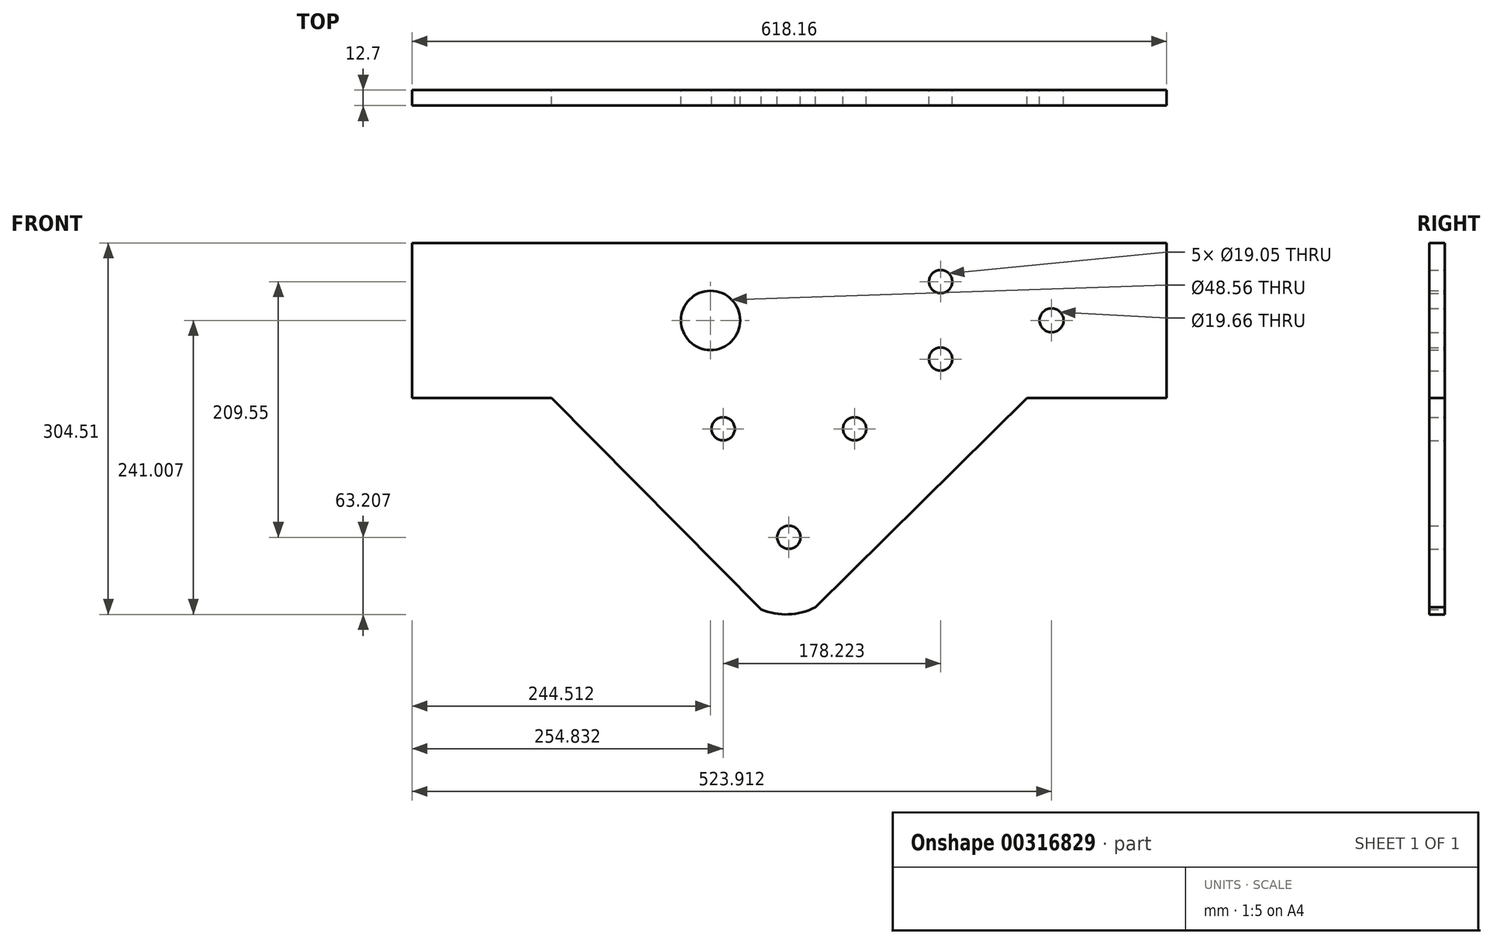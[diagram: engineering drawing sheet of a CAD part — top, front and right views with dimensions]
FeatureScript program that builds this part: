
annotation { "Feature Type Name" : "Feature", "Feature Type Description" : "" }
export const myFeature = defineFeature(function(context is Context, id is Id, definition is map)
    precondition{}
    {
        {
            var Q0;
            Q0=qCreatedBy(makeId("Front.planeOp"),FACE);
            var sketch = newSketch(context, id + "F0", { "sketchPlane" : qUnion([Q0])});
            skLineSegment(sketch, "E0.bottom", {"start": v(-308.68, 55.52) * mm, "end": v(-194.38, 55.52) * mm});
            skLineSegment(sketch, "E0.top", {"start": v(-308.68, 182.52) * mm, "end": v(309.48, 182.52) * mm});
            skLineSegment(sketch, "E0.left", {"start": v(-308.68, 55.52) * mm, "end": v(-308.68, 182.52) * mm});
            skLineSegment(sketch, "E0.right", {"start": v(309.48, 55.52) * mm, "end": v(309.48, 182.52) * mm});
            skLineSegment(sketch, "E1", {"start": v(-158.49, 19.24) * mm, "end": v(-22.68, -118.05) * mm});
            skArc(sketch, "E2", {"start": v(-22.68, -118.05) * mm, "mid": v(-0.3, -121.94) * mm, "end": v(21.65, -116.14) * mm});
            skLineSegment(sketch, "E3.trimOffspring", {"start": v(195.18, 55.52) * mm, "end": v(309.48, 55.52) * mm});
            skCircle(sketch, "E4", {"center": v(-64.17, 119.02) * mm, "radius": 24.28 * mm});
            skCircle(sketch, "E5.MirrorC", {"center": v(215.23, 119.02) * mm, "radius": 9.83 * mm});
            skLineSegment(sketch, "E6.MirrorCS", {"start": v(195.18, 55.52) * mm, "end": v(21.65, -116.14) * mm});
            skLineSegment(sketch, "E7", {"start": v(-308.68, 87.27) * mm, "end": v(309.48, 87.27) * mm, "construction": true});
            skLineSegment(sketch, "E8", {"start": v(-308.68, 150.77) * mm, "end": v(309.48, 150.77) * mm, "construction": true});
            skLineSegment(sketch, "E9", {"start": v(0, 0) * mm, "end": v(0, 29.21) * mm});
            skLineSegment(sketch, "E10.0", {"start": v(53.85, 0) * mm, "end": v(53.85, 30.12) * mm});
            skCircle(sketch, "E11", {"center": v(53.85, 30.12) * mm, "radius": 9.53 * mm});
            skPoint(sketch, "E12.center.orphan", {"position": v(0, -52.58) * mm});
            skCircle(sketch, "E13", {"center": v(0, -58.78) * mm, "radius": 9.52 * mm});
            skCircle(sketch, "E14.MirrorC", {"center": v(-53.85, 30.12) * mm, "radius": 9.53 * mm});
            skLineSegment(sketch, "E15", {"start": v(-158.49, 19.24) * mm, "end": v(-194.38, 55.52) * mm});
            skCircle(sketch, "E16", {"center": v(-345.66, 150.77) * mm, "radius": 9.53 * mm});
            skCircle(sketch, "E17", {"center": v(-345.66, 87.27) * mm, "radius": 9.53 * mm});
            skCircle(sketch, "E18", {"center": v(124.37, 150.77) * mm, "radius": 9.53 * mm});
            skCircle(sketch, "E19", {"center": v(124.37, 87.27) * mm, "radius": 9.53 * mm});
            skLineSegment(sketch, "E20", {"start": v(-64.17, 119.02) * mm, "end": v(-308.68, 119.02) * mm, "construction": true});
            skLineSegment(sketch, "E21", {"start": v(215.23, 119.02) * mm, "end": v(309.48, 119.02) * mm, "construction": true});
            skSolve(sketch);
        }
        {
            var Q0;
            Q0=makeQuery(id+"F0.imprint","IMPRINT",FACE,{"disambiguationData":[TD([[makeQuery(id+"F0.imprint","IMPRINT",EDGE,{"derivedFrom":sQuery(id+"F0.wireOp",EDGE,"E0.bottom")}),1.0]])]});
            extrude(context, id + "F1", {"entities" : qUnion([Q0]), "depth" : 12.7 * mm});
        }
    });
